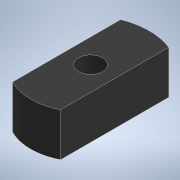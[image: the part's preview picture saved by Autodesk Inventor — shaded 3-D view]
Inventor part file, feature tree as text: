
AUTODESK INVENTOR PART (.ipt)
format: ipt  version: 2021 (Build 250183000, 183)  size: 101,888 bytes
history: native  units: mm
features: extrude x2, sketch x2
ambient origin geometry x8: Origin, YZ Plane, XZ Plane, XY Plane, X Axis, Y Axis, Z Axis, Center Point
bodies: Solid1 (feature_tree)
feature tree (4):
  extrude  "Extrusion1"  Depth=5.0mm
  extrude  "Extrusion3"  Depth=9.0mm
  sketch  "Sketch1"  dims[d0=22.0mm d1=5.0mm]
  sketch  "Sketch2"  dims[d2=9.0mm d3=0.0mm d7=22.5mm d8=11.25mm d9=5.0mm d10=9.0mm d11=0.0mm]
